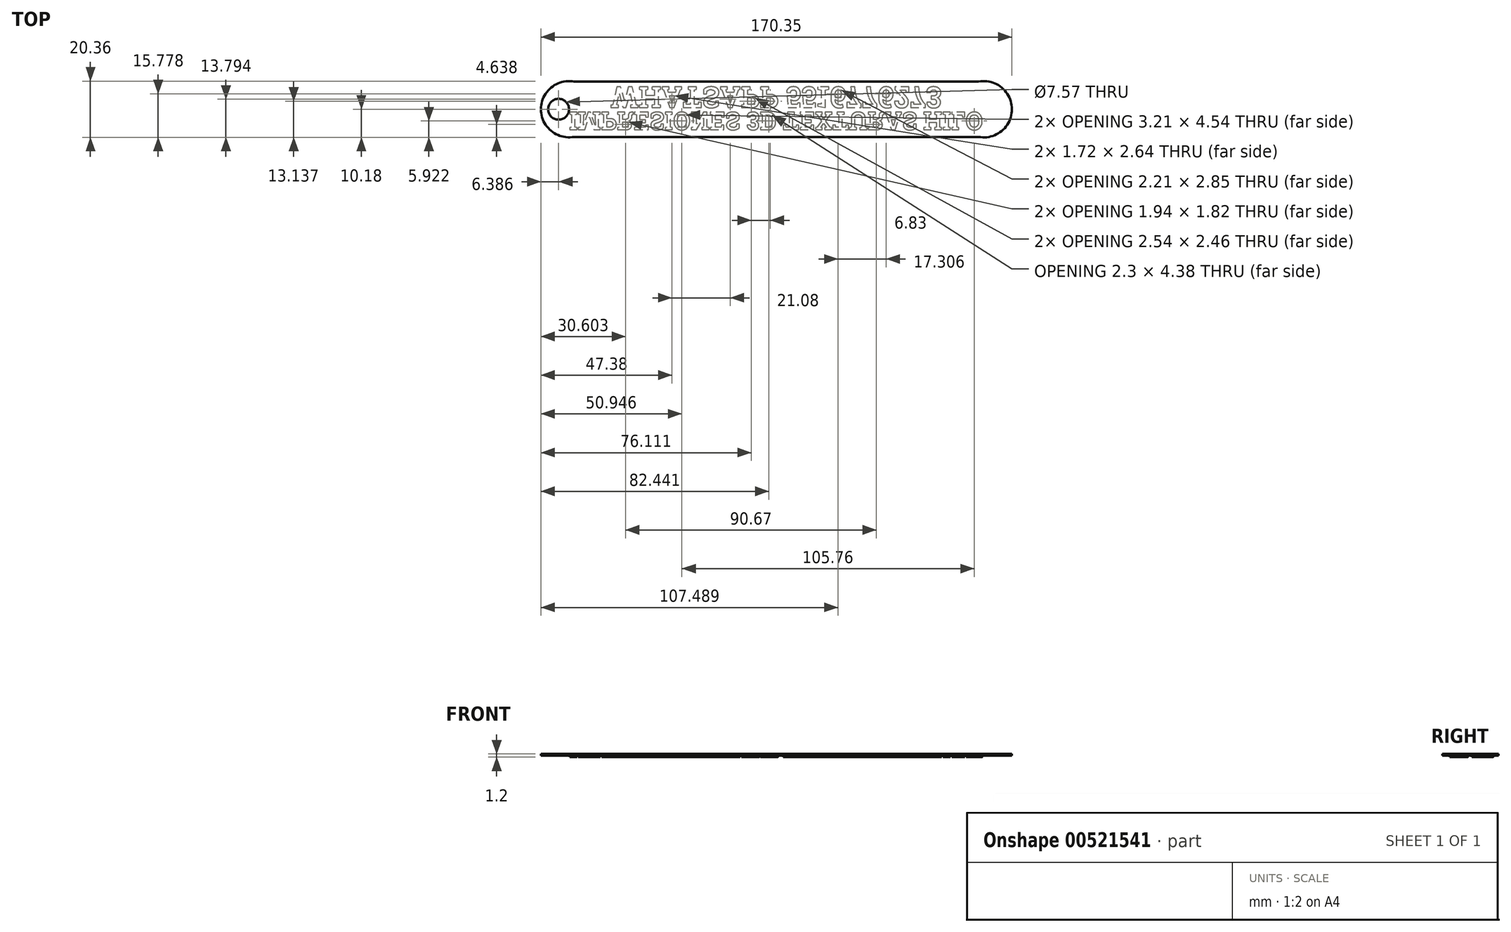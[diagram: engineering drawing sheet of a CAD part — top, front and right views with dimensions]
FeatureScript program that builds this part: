
annotation { "Feature Type Name" : "Feature", "Feature Type Description" : "" }
export const myFeature = defineFeature(function(context is Context, id is Id, definition is map)
    precondition{}
    {
        {
            var Q0;
            Q0=qCreatedBy(makeId("Top.planeOp"),FACE);
            var sketch = newSketch(context, id + "F0", { "sketchPlane" : qUnion([Q0])});
            skLineSegment(sketch, "E0.bottom", {"start": v(-75, 10) * mm, "end": v(75, 10) * mm});
            skLineSegment(sketch, "E0.top", {"start": v(-75, -10) * mm, "end": v(75, -10) * mm});
            skLineSegment(sketch, "E0.left", {"start": v(-75, 10) * mm, "end": v(-75, -10) * mm});
            skLineSegment(sketch, "E0.right", {"start": v(75, 10) * mm, "end": v(75, -10) * mm});
            skCircle(sketch, "E1", {"center": v(-75, 0) * mm, "radius": 10.17 * mm});
            skCircle(sketch, "E2", {"center": v(75, 0) * mm, "radius": 10.18 * mm});
            skCircle(sketch, "E3", {"center": v(-78.78, 0) * mm, "radius": 3.78 * mm});
            skSolve(sketch);
        }
        {
            var Q0;
            Q0 = qSketchRegion(id + "F0", true);
            extrude(context, id + "F1", {"entities" : qUnion([Q0]), "oppositeDirection" : true, "depth" : .6 * mm, "offsetDistance" : 25 * mm});
        }
        {
            var Q0;
            Q0=makeQuery(id+"F1.opExtrude","CAP_FACE",FACE,{"disambiguationData":[OSD([sQuery(id+"F0.wireOp",EDGE,"E0.bottom"),sQuery(id+"F0.wireOp",EDGE,"E0.top"),sQuery(id+"F0.wireOp",EDGE,"E0.left"),sQuery(id+"F0.wireOp",EDGE,"E0.right")])],"isStart":false});
            var sketch = newSketch(context, id + "F2", { "sketchPlane" : qUnion([Q0])});
            skText(sketch, "E4", { "text": "IMPRESIONES 3D TEXTURAS HILO", "fontName": "RobotoSlab-Bold.ttf"});
            skText(sketch, "E5", { "text": "WHATSAPP 5516776273", "fontName": "RobotoSlab-Bold.ttf"});
            const initialGuessF2  = {"E4": [-0.075, 0.00109, 1, 0, 0.00642], "E5": [-0.06, -0.00807, 1, 0, 0.0076]};
            skSetInitialGuess(sketch, initialGuessF2);
            skSolve(sketch);
        }
        {
            var Q0;
            Q0 = qSketchRegion(id + "F2", true);
            extrude(context, id + "F3", {"entities" : qUnion([Q0]), "depth" : .6 * mm, "offsetDistance" : 25 * mm});
        }
    });
